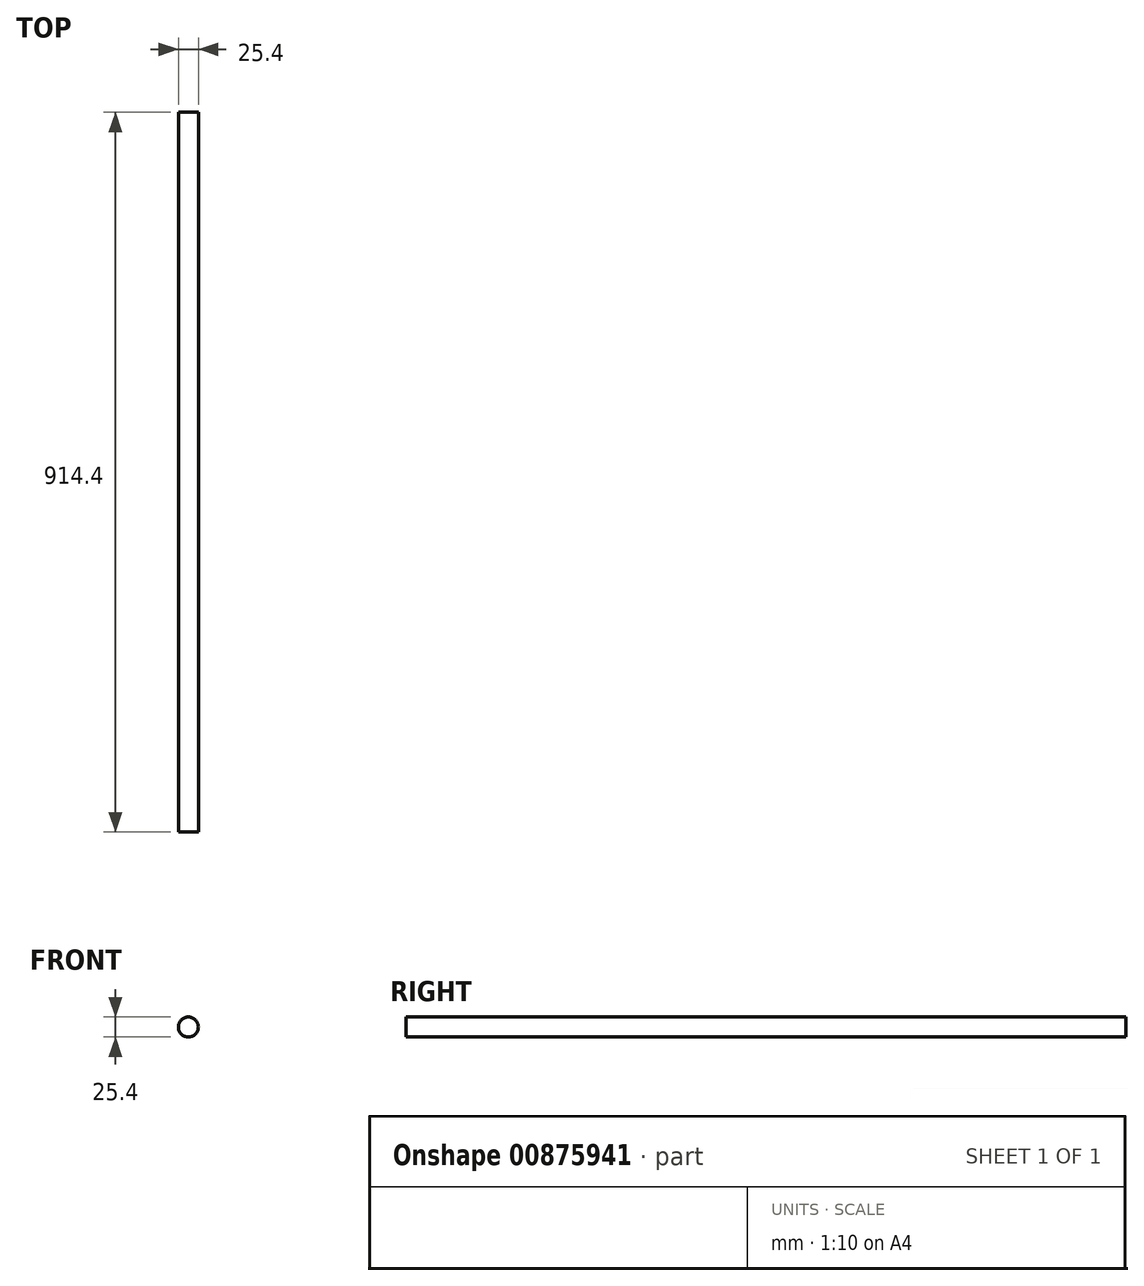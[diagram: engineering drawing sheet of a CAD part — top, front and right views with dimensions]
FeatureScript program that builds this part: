
annotation { "Feature Type Name" : "Feature", "Feature Type Description" : "" }
export const myFeature = defineFeature(function(context is Context, id is Id, definition is map)
    precondition{}
    {
        {
            var Q0;
            Q0=qCreatedBy(makeId("Front.planeOp"),FACE);
            var sketch = newSketch(context, id + "F0", { "sketchPlane" : qUnion([Q0])});
            skCircle(sketch, "E0", {"center": v(0, 0) * mm, "radius": 12.7 * mm});
            skSolve(sketch);
        }
        {
            var Q0;
            Q0=qSketchRegion(id+"F0",true);
            extrude(context, id + "F1", {"entities" : qUnion([Q0]), "oppositeDirection" : true, "depth" : 914.4 * mm});
        }
    });
